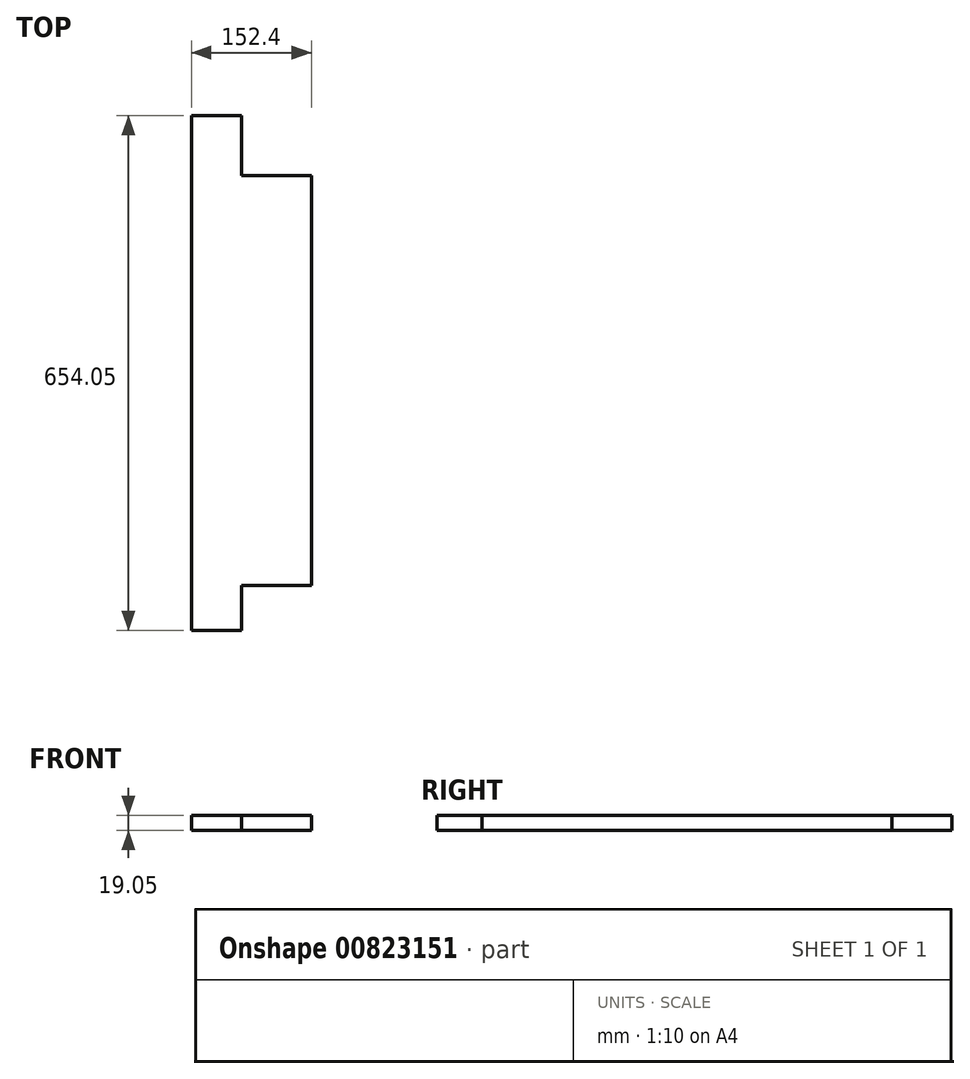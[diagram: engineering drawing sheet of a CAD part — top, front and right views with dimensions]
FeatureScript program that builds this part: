
annotation { "Feature Type Name" : "Feature", "Feature Type Description" : "" }
export const myFeature = defineFeature(function(context is Context, id is Id, definition is map)
    precondition{}
    {
        {
            var Q0;
            Q0=qCreatedBy(makeId("Top.planeOp"),FACE);
            var sketch = newSketch(context, id + "F0", { "sketchPlane" : qUnion([Q0])});
            skLineSegment(sketch, "E0.bottom", {"start": v(0, 0) * mm, "end": v(63.5, 0) * mm});
            skLineSegment(sketch, "E0.top", {"start": v(0, 654.05) * mm, "end": v(63.5, 654.05) * mm});
            skLineSegment(sketch, "E0.left", {"start": v(0, 0) * mm, "end": v(0, 654.05) * mm});
            skLineSegment(sketch, "E0.right", {"start": v(152.4, 57.15) * mm, "end": v(152.4, 577.85) * mm});
            skLineSegment(sketch, "E1.top", {"start": v(152.4, 577.85) * mm, "end": v(63.5, 577.85) * mm});
            skLineSegment(sketch, "E1.right", {"start": v(63.5, 654.05) * mm, "end": v(63.5, 577.85) * mm});
            skLineSegment(sketch, "E2.top", {"start": v(152.4, 57.15) * mm, "end": v(63.5, 57.15) * mm});
            skLineSegment(sketch, "E2.right", {"start": v(63.5, 0) * mm, "end": v(63.5, 57.15) * mm});
            skSolve(sketch);
        }
        {
            var Q0;
            Q0 = qSketchRegion(id + "F0", true);
            extrude(context, id + "F1", {"entities" : qUnion([Q0]), "depth" : 19.05 * mm, "offsetDistance" : 25.4 * mm});
        }
    });
